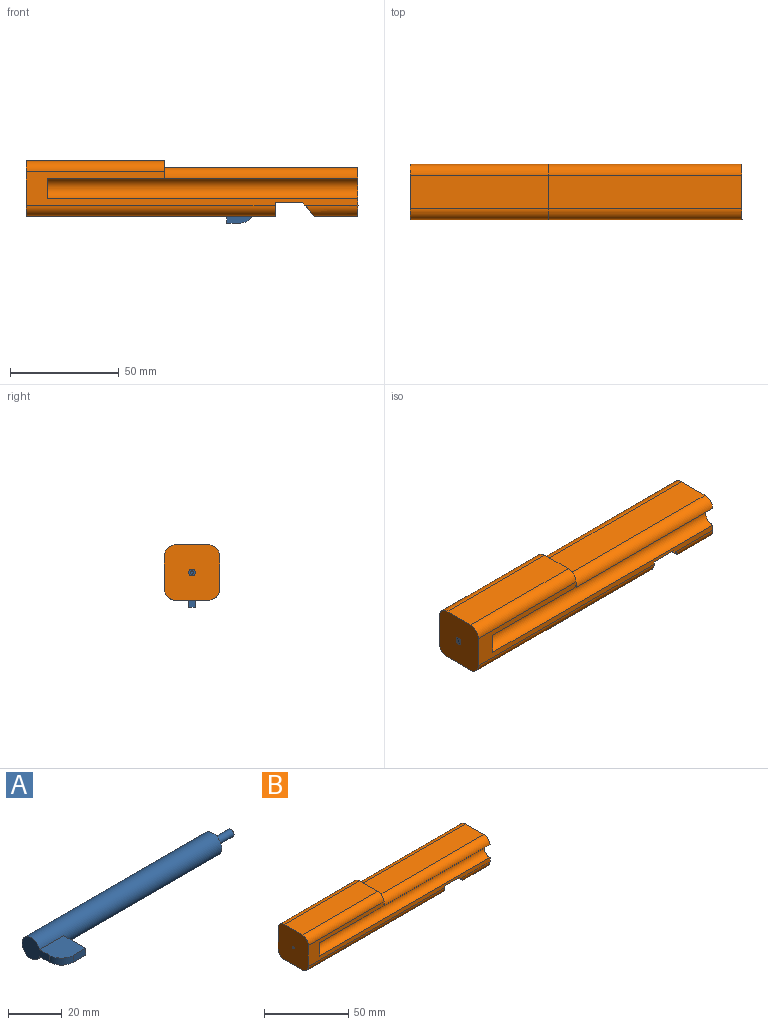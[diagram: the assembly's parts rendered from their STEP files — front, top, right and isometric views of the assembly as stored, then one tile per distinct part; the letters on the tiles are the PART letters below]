
ASSEMBLY  parts=2 mates=1
PART A: 10 faces, bbox 104.9x20.6x9.5 mm
  f0: plane 3.18x3.18mm, normal (1,0,0), area 7.9mm2, adj f1
  f1: cylinder r=1.59mm len=9.65mm, axis (1,0,0), area 96.3mm2, adj f0,f2
  f2: plane 9.53x9.53mm, normal (1,0,0), area 63.3mm2, adj f1,f3
  f3: cylinder r=4.76mm len=95.25mm, axis (1,0,0), area 2809.1mm2, adj f2,f4,f5,f7,f8
  f4: plane 14.29x9.53mm, normal (-1,0,0), area 86.7mm2, adj f3,f7,f8,f9
  f5: plane 11.39x3.18mm, normal (1,0,0), area 35.6mm2, adj f3,f6,f7,f8
  f6: plane 6.35x3.18mm, normal (0,-1,0), area 20.2mm2, adj f5,f7,f8,f9
  f7: plane 12.7x11.39mm, normal (0,0,1), area 135.9mm2, adj f3,f4,f5,f6,f9
  f8: plane 12.7x11.39mm, normal (0,0,-1), area 135.9mm2, adj f3,f4,f5,f6,f9
  f9: cylinder r=6.35mm len=6.35mm, axis (0,0,-1), area 31.7mm2, adj f4,f6,f7,f8
PART B: 34 faces, bbox 152.4x25.4x25.4 mm
  f0: plane 20.15x6.03mm, normal (0,0,-1), area 121.6mm2, adj f6,f13,f25,f31
  f1: plane 114.3x15.24mm, normal (0,0,-1), area 1671.4mm2, adj f2,f10,f11,f23,f26,f31,f32,f33
  f2: plane 11.11x6.35mm, normal (1,0,0), area 65mm2, adj f1,f3,f5,f26,f32
  f3: plane 12.7x11.11mm, normal (0,0,-1), area 141.1mm2, adj f2,f4,f5,f32
  f4: plane 11.11x6.35mm, normal (-0.77,0,-0.64), area 84.4mm2, adj f3,f5,f14,f28,f32
  f5: plane 152.4x15.24mm, normal (0,-1,0), area 690.9mm2, adj f2,f3,f4,f6,f8,f10,f21,f22
  f6: plane 25.4x22.23mm, normal (1,0,0), area 374.5mm2, adj f0,f5,f7,f14,f15,f16,f19,f21
  f7: plane 88.9x15.26mm, normal (0,0,1), area 1356.6mm2, adj f6,f8,f24,f27
  f8: plane 25.4x7.94mm, normal (1,0,0), area 80.5mm2, adj f5,f7,f9,f15,f24,f27,f29,f30
  f9: plane 63.5x15.24mm, normal (0,0,1), area 967.7mm2, adj f8,f10,f29,f30
  f10: plane 25.4x25.4mm, normal (-1,0,0), area 621mm2, adj f1,f5,f9,f15,f18,f23,f26,f29
  f11: plane 11.11x6.35mm, normal (1,0,0), area 65mm2, adj f1,f12,f15,f23,f31
  f12: plane 12.7x11.11mm, normal (0,0,-1), area 141.1mm2, adj f11,f13,f15,f31
  f13: plane 11.11x6.35mm, normal (-0.77,0,-0.64), area 84.4mm2, adj f0,f12,f15,f25,f31
  f14: plane 20.15x6.03mm, normal (0,0,-1), area 121.6mm2, adj f4,f6,f28,f32
  f15: plane 152.4x15.24mm, normal (0,1,0), area 690.9mm2, adj f6,f8,f10,f11,f12,f13,f19,f20
  f16: cylinder r=4.76mm len=142.88mm, axis (1,0,0), area 4080.1mm2, adj f6,f17,f31,f32,f33
  f17: plane 9.53x9.53mm, normal (1,0,0), area 69.3mm2, adj f16,f18
  f18: cylinder r=0.79mm len=9.53mm, axis (-1,0,0), area 47.5mm2, adj f10,f17
  f19: cylinder r=4.76mm len=142.88mm, axis (1,0,0), area 2137.7mm2, adj f6,f15,f20,f24
  f20: plane 9.53x4.76mm, normal (1,0,0), area 35.6mm2, adj f15,f19
  f21: cylinder r=4.76mm len=142.88mm, axis (1,0,0), area 2137.7mm2, adj f5,f6,f22,f27
  f22: plane 9.53x4.76mm, normal (1,0,0), area 35.6mm2, adj f5,f21
  f23: cylinder r=5.08mm len=114.3mm, axis (1,0,0), area 912.1mm2, adj f1,f10,f11,f15
  f24: cylinder r=5.08mm len=88.9mm, axis (1,0,0), area 681.1mm2, adj f6,f7,f8,f19
  f25: cylinder r=5.08mm len=24.35mm, axis (1,0,0), area 173mm2, adj f0,f6,f13,f15
  f26: cylinder r=5.08mm len=114.3mm, axis (-1,0,0), area 912.1mm2, adj f1,f2,f5,f10
  f27: cylinder r=5.08mm len=88.9mm, axis (1,0,0), area 681.1mm2, adj f6,f7,f8,f21
  f28: cylinder r=5.08mm len=24.35mm, axis (-1,0,0), area 173mm2, adj f4,f5,f6,f14
  f29: cylinder r=5.08mm len=63.5mm, axis (-1,0,0), area 506.7mm2, adj f8,f9,f10,f15
  f30: cylinder r=5.08mm len=63.5mm, axis (1,0,0), area 506.7mm2, adj f5,f8,f9,f10
  f31: plane 60.33x8.21mm, normal (0,-1,0), area 398mm2, adj f0,f1,f6,f11,f12,f13,f16,f33
  f32: plane 60.33x8.21mm, normal (0,1,0), area 398mm2, adj f1,f2,f3,f4,f6,f14,f16,f33
  f33: plane 8.21x3.18mm, normal (1,0,0), area 25.5mm2, adj f1,f16,f31,f32
PLACE A rot(axis=(0,-0.71,-0.71),180deg) t=(-24.36,-2.88,-18.29)mm
PLACE B t=(12.13,-2.88,-3.25)mm fixed
MATE slider A.f5 <-> B.f33  axis (-1,0,0) through (20.29,-1.29,4.96)mm
